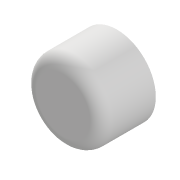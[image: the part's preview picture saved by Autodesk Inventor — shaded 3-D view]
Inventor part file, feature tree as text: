
AUTODESK INVENTOR PART (.ipt)
format: ipt  version: 2020.3 (Build 243373000, 373)  size: 115,200 bytes
history: native  units: mm
features: other x3, extrude x2, sketch x2, thread x1, fillet x1, reference x1
ambient origin geometry x8: Origin, YZ Plane, XZ Plane, XY Plane, X Axis, Y Axis, Z Axis, Center Point
bodies: Volumenkörper1 (feature_tree)
feature tree (10):
  extrude  "Extrusion1"  Depth=7.0mm TaperAngle=0.0deg
  thread  "Gewinde1"  [1 undecoded]
  extrude  "Extrusion2"  Depth=2.0mm
  fillet  "Rundung1"  [1 undecoded]
  sketch  "Skizze1"  dims[d0=13.0mm d1=7.0mm d2=0.0mm d3=7.0mm d4=0.0mm]
  reference  "Referenz1"
  sketch  "Skizze2"  dims[d5=2.0mm d6=0.0mm d7=2.0mm]
  other  "<userpath>\SynologyDrive\WiMi\RobotikMaschinen\HeleneRoboterarm\KraftMessNadel\Gesamt.iam"
  other  "Gesamt.iam"
  other  "NadelHalterLose:1"
note: 2 required parameter values undecoded (feature->parameter linkage not recoverable at this tier; creation-order binding heuristic only, values carry confidence <= 0.55)
